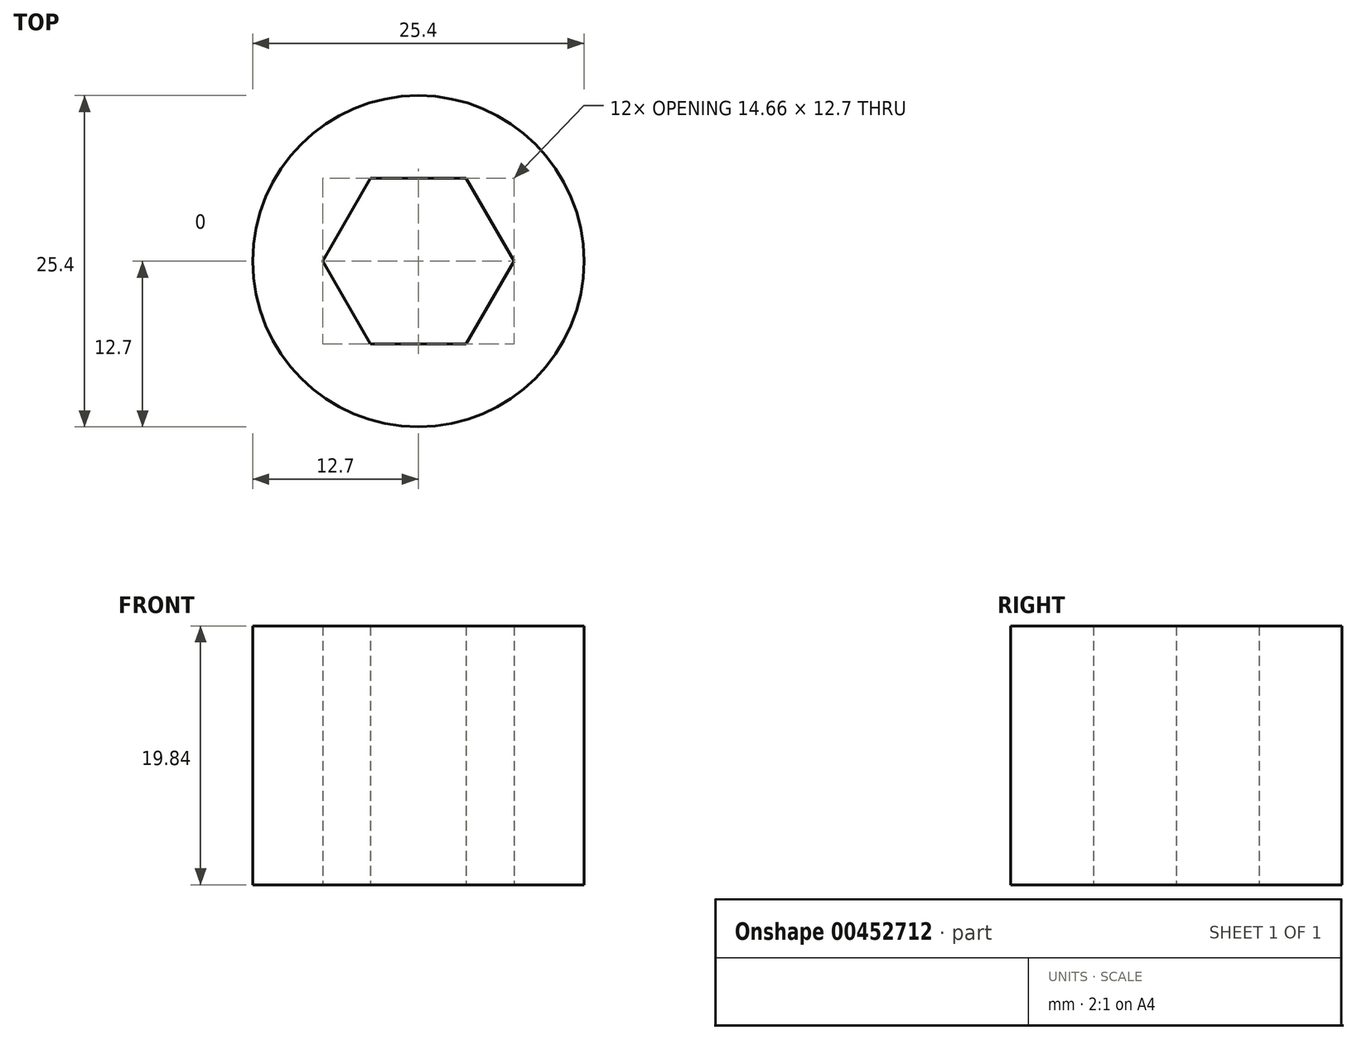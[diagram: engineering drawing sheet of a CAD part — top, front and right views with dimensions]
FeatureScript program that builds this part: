
annotation { "Feature Type Name" : "Feature", "Feature Type Description" : "" }
export const myFeature = defineFeature(function(context is Context, id is Id, definition is map)
    precondition{}
    {
        {
            var Q0;
            Q0=qCreatedBy(makeId("Top.planeOp"),FACE);
            var sketch = newSketch(context, id + "F0", { "sketchPlane" : qUnion([Q0])});
            skCircle(sketch, "E0", {"center": v(0, 0) * mm, "radius": 12.7 * mm});
            skCircle(sketch, "E1.cCircle", {"center": v(0, 0) * mm, "radius": 6.35 * mm, "construction": true});
            skLineSegment(sketch, "E1.0", {"start": v(-3.67, 6.35) * mm, "end": v(3.67, 6.35) * mm});
            skLineSegment(sketch, "E1.1", {"start": v(3.67, 6.35) * mm, "end": v(7.33, 0) * mm});
            skLineSegment(sketch, "E1.2", {"start": v(7.33, 0) * mm, "end": v(3.67, -6.35) * mm});
            skLineSegment(sketch, "E1.3", {"start": v(3.67, -6.35) * mm, "end": v(-3.67, -6.35) * mm});
            skLineSegment(sketch, "E1.4", {"start": v(-3.67, -6.35) * mm, "end": v(-7.33, 0) * mm});
            skLineSegment(sketch, "E1.5", {"start": v(-7.33, 0) * mm, "end": v(-3.67, 6.35) * mm});
            skPoint(sketch, "E1.0.midPoint", {"position": v(0, 6.35) * mm});
            skSolve(sketch);
        }
        {
            var Q0;
            Q0 = qSketchRegion(id + "F0", true);
            extrude(context, id + "F1", {"entities" : qUnion([Q0]), "depth" : 19.84 * mm});
        }
    });
